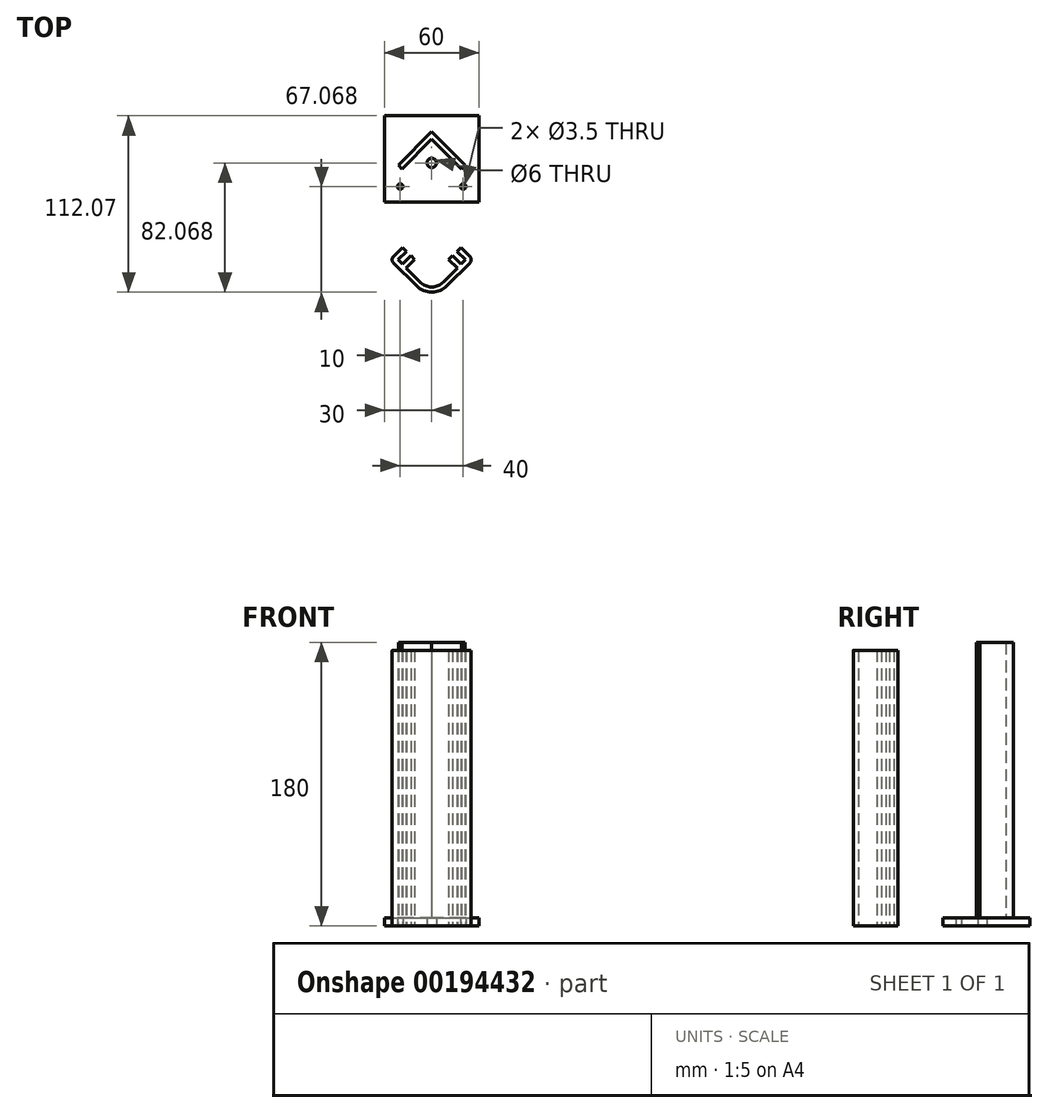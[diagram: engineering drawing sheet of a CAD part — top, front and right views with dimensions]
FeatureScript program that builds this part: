
annotation { "Feature Type Name" : "Feature", "Feature Type Description" : "" }
export const myFeature = defineFeature(function(context is Context, id is Id, definition is map)
    precondition{}
    {
        {
            var Q0;
            Q0=qCreatedBy(makeId("Top.planeOp"),FACE);
            var sketch = newSketch(context, id + "F0", { "sketchPlane" : qUnion([Q0])});
            skLineSegment(sketch, "E0.bottom", {"start": v(-30, 43.69) * mm, "end": v(30, 43.69) * mm});
            skLineSegment(sketch, "E0.top", {"start": v(-30, -11.31) * mm, "end": v(30, -11.31) * mm});
            skLineSegment(sketch, "E0.left", {"start": v(-30, 43.69) * mm, "end": v(-30, -11.31) * mm});
            skLineSegment(sketch, "E0.right", {"start": v(30, 43.69) * mm, "end": v(30, -11.31) * mm});
            skLineSegment(sketch, "E1", {"start": v(-21.21, 12.22) * mm, "end": v(0, 33.43) * mm});
            skLineSegment(sketch, "E2", {"start": v(0, 33.43) * mm, "end": v(21.21, 12.22) * mm});
            skLineSegment(sketch, "E3", {"start": v(21.21, 12.22) * mm, "end": v(18.84, 9.85) * mm});
            skLineSegment(sketch, "E4", {"start": v(18.84, 9.85) * mm, "end": v(0, 28.69) * mm});
            skLineSegment(sketch, "E5", {"start": v(0, 28.69) * mm, "end": v(-18.84, 9.85) * mm});
            skLineSegment(sketch, "E6", {"start": v(-18.84, 9.85) * mm, "end": v(-21.21, 12.22) * mm});
            skCircle(sketch, "E7", {"center": v(-20, -1.31) * mm, "radius": 1.75 * mm});
            skCircle(sketch, "E8", {"center": v(0, 13.69) * mm, "radius": 3 * mm});
            skCircle(sketch, "E9", {"center": v(20, -1.31) * mm, "radius": 1.75 * mm});
            skLineSegment(sketch, "E10", {"start": v(-18.57, -39.98) * mm, "end": v(-16.1, -42.46) * mm});
            skLineSegment(sketch, "E11", {"start": v(-16.1, -42.46) * mm, "end": v(-21.4, -47.76) * mm});
            skLineSegment(sketch, "E12", {"start": v(-21.4, -47.76) * mm, "end": v(-18.57, -50.59) * mm});
            skLineSegment(sketch, "E13", {"start": v(-18.57, -50.59) * mm, "end": v(-13.27, -45.29) * mm});
            skLineSegment(sketch, "E14", {"start": v(-13.27, -45.29) * mm, "end": v(-10.8, -47.76) * mm});
            skLineSegment(sketch, "E15", {"start": v(-10.8, -47.76) * mm, "end": v(-16.25, -53.22) * mm});
            skLineSegment(sketch, "E16", {"start": v(-26.35, -47.76) * mm, "end": v(-18.57, -39.98) * mm});
            skLineSegment(sketch, "E17", {"start": v(-16.25, -53.22) * mm, "end": v(-7.46, -62.01) * mm});
            skLineSegment(sketch, "E18", {"start": v(-26.35, -47.76) * mm, "end": v(-9.78, -64.33) * mm});
            skLineSegment(sketch, "E19.MirrorCS", {"start": v(16.25, -53.22) * mm, "end": v(7.46, -62.01) * mm});
            skLineSegment(sketch, "E20.MirrorCS", {"start": v(26.35, -47.76) * mm, "end": v(9.78, -64.33) * mm});
            skLineSegment(sketch, "E21.MirrorCS", {"start": v(10.8, -47.76) * mm, "end": v(16.25, -53.22) * mm});
            skLineSegment(sketch, "E22.MirrorCS", {"start": v(13.27, -45.29) * mm, "end": v(10.8, -47.76) * mm});
            skLineSegment(sketch, "E23.MirrorCS", {"start": v(18.57, -50.59) * mm, "end": v(13.27, -45.29) * mm});
            skLineSegment(sketch, "E24.MirrorCS", {"start": v(21.4, -47.76) * mm, "end": v(18.57, -50.59) * mm});
            skLineSegment(sketch, "E25.MirrorCS", {"start": v(26.35, -47.76) * mm, "end": v(18.57, -39.98) * mm});
            skLineSegment(sketch, "E26.MirrorCS", {"start": v(18.57, -39.98) * mm, "end": v(16.1, -42.46) * mm});
            skLineSegment(sketch, "E27.MirrorCS", {"start": v(16.1, -42.46) * mm, "end": v(21.4, -47.76) * mm});
            skArc(sketch, "E28", {"start": v(-7.46, -62.01) * mm, "mid": v(0, -65.1) * mm, "end": v(7.46, -62.01) * mm});
            skArc(sketch, "E29", {"start": v(-9.78, -64.33) * mm, "mid": v(0, -68.38) * mm, "end": v(9.78, -64.33) * mm});
            skPoint(sketch, "E30.MirrorCS.end.orphan", {"position": v(7.46, -62.01) * mm});
            skLineSegment(sketch, "E31", {"start": v(-75.8, 48.69) * mm, "end": v(75.06, 48.69) * mm, "construction": true});
            skSolve(sketch);
        }
        {
            var Q0;
            Q0=makeQuery(id+"F0.imprint","IMPRINT",FACE,{"disambiguationData":[TD([[makeQuery(id+"F0.imprint","IMPRINT",EDGE,{"derivedFrom":sQuery(id+"F0.wireOp",EDGE,"E0.bottom")}),-1.0]])]});
            extrude(context, id + "F1", {"entities" : qUnion([Q0]), "depth" : 5 * mm});
        }
        {
            var Q0;
            Q0=makeQuery(id+"F0.imprint","IMPRINT",FACE,{"disambiguationData":[TD([[makeQuery(id+"F0.imprint","IMPRINT",EDGE,{"derivedFrom":sQuery(id+"F0.wireOp",EDGE,"E1")}),-1.0]])]});
            extrude(context, id + "F2", {"entities" : qUnion([Q0]), "operationType" : NewBodyOperationType.ADD, "depth" : 180 * mm});
        }
        {
            var Q0;
            {var subQ6=sQuery(id+"F0.wireOp",EDGE,"E11");Q0=makeQuery(id+"F0.imprint","IMPRINT",FACE,{"disambiguationData":[TD([[makeQuery(id+"F0.imprint","IMPRINT",EDGE,{"derivedFrom":subQ6}),-1.0]])]});}
            extrude(context, id + "F3", {"entities" : qUnion([Q0]), "depth" : 175 * mm});
        }
        {
            var Q0;
            Q0=makeQuery(id+"F3.opExtrude","SWEPT_EDGE",EDGE,{"disambiguationData":[OSD([sQuery(id+"F0.wireOp",EDGE,"E20.MirrorCS"),sQuery(id+"F0.wireOp",EDGE,"E25.MirrorCS")])]});
            var Q1;
            Q1=makeQuery(id+"F3.opExtrude","SWEPT_EDGE",EDGE,{"disambiguationData":[OSD([sQuery(id+"F0.wireOp",EDGE,"E16"),sQuery(id+"F0.wireOp",EDGE,"E18")])]});
            fillet(context, id + "F4", {"entities" : qUnion([Q0, Q1]), "radius" : 3 * mm, "tangentPropagation" : true, "allowEdgeOverflow" : false});
        }
    });
